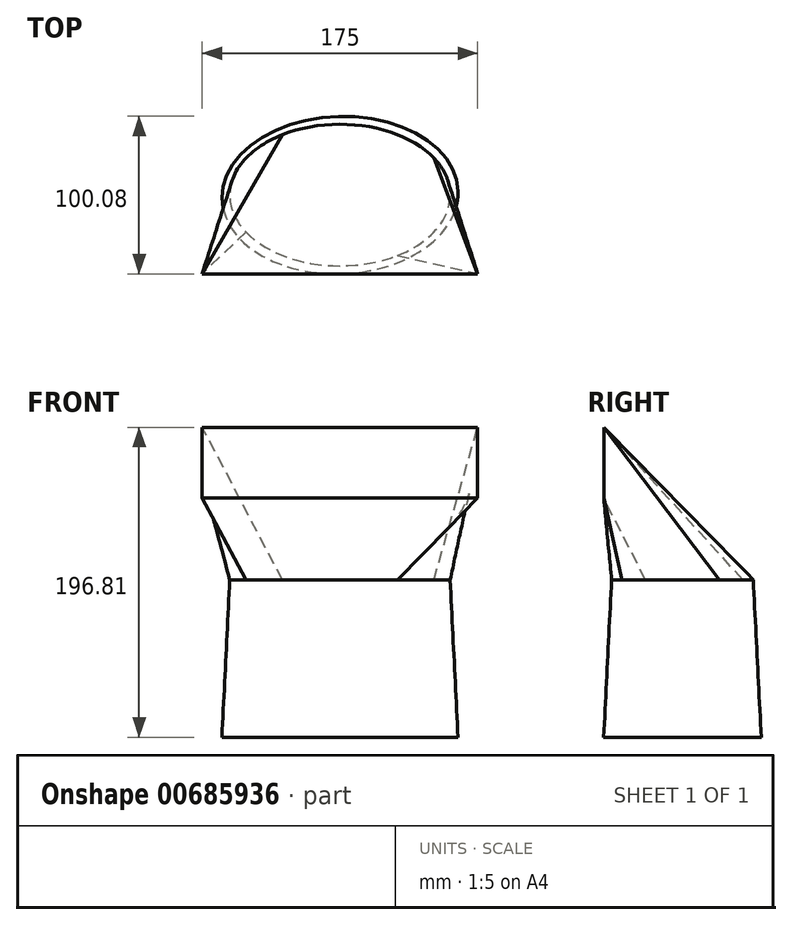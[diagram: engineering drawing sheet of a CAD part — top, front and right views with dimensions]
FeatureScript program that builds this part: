
annotation { "Feature Type Name" : "Feature", "Feature Type Description" : "" }
export const myFeature = defineFeature(function(context is Context, id is Id, definition is map)
    precondition{}
    {
        {
            assignVariable(context, id + "F0", {"name" : "X", "anyValue" : 1});
        }
        {
            var Q0;
            Q0=qCreatedBy(makeId("Top.planeOp"),FACE);
            var sketch = newSketch(context, id + "F1", { "sketchPlane" : qUnion([Q0])});
            skEllipse(sketch, "E0", {"center": v(0, 0) * mm, "majorRadius": 75 * mm, "minorRadius": 50 * mm, "majorAxis": v(1, 0.04)});
            skSolve(sketch);
        }
        {
            var Q0;
            Q0=qCreatedBy(makeId("Top.planeOp"),FACE);
            cPlane(context, id + "F2", {"entities" : qUnion([Q0]), "cplaneType" : CPlaneType.OFFSET, "offset" : (getVariable(context, 'X') * 100) * mm, "width" : 150 * mm, "height" : 150 * mm});
        }
        {
            var Q0;
            Q0=qCreatedBy(id+"F2.planeOp",FACE);
            var sketch = newSketch(context, id + "F3", { "sketchPlane" : qUnion([Q0])});
            skEllipse(sketch, "E1", {"center": v(0, 0) * mm, "majorRadius": 70 * mm, "minorRadius": 45 * mm, "majorAxis": v(-1, 0)});
            skSolve(sketch);
        }
        {
            var Q0;
            Q0=makeQuery(id+"F1.imprint","IMPRINT",FACE,{"disambiguationData":[TD([[makeQuery(id+"F1.imprint","IMPRINT",EDGE,{"derivedFrom":sQuery(id+"F1.wireOp",EDGE,"E0")}),1.0]])]});
            var Q1;
            Q1=makeQuery(id+"F3.imprint","IMPRINT",FACE,{"disambiguationData":[TD([[makeQuery(id+"F3.imprint","IMPRINT",EDGE,{"derivedFrom":sQuery(id+"F3.wireOp",EDGE,"E1")}),1.0]])]});
            loft(context, id + "F4", {"sheetProfilesArray" : [{ "sheetProfileEntities" : qUnion([Q0]) }, { "sheetProfileEntities" : qUnion([Q1]) }]});
        }
        {
            var Q0;
            Q0=qCreatedBy(makeId("Front.planeOp"),FACE);
            var sketch = newSketch(context, id + "F5", { "sketchPlane" : qUnion([Q0])});
            skLineSegment(sketch, "E2.bottom", {"start": v(-87.5, 196.8) * mm, "end": v(87.5, 196.8) * mm});
            skLineSegment(sketch, "E2.top", {"start": v(-87.5, 151.8) * mm, "end": v(87.5, 151.8) * mm});
            skLineSegment(sketch, "E2.left", {"start": v(-87.5, 196.8) * mm, "end": v(-87.5, 151.8) * mm});
            skLineSegment(sketch, "E2.right", {"start": v(87.5, 196.8) * mm, "end": v(87.5, 151.8) * mm});
            skPoint(sketch, "E3", {"position": v(-63.7, 88.78) * mm});
            skLineSegment(sketch, "E4", {"start": v(0, 196.8) * mm, "end": v(0, 151.8) * mm});
            skLineSegment(sketch, "E5", {"start": v(0, 174.3) * mm, "end": v(87.5, 174.3) * mm});
            skLineSegment(sketch, "E6", {"start": v(0, 174.3) * mm, "end": v(-87.5, 174.3) * mm});
            skSolve(sketch);
        }
        {
            var Q0;
            {var subQ5=sQuery(id+"F5.wireOp",EDGE,"E5");Q0=makeQuery(id+"F5.imprint","IMPRINT",FACE,{"disambiguationData":[TD([[makeQuery(id+"F5.imprint","IMPRINT",EDGE,{"derivedFrom":subQ5}),-1.0]])]});}
            cPlane(context, id + "F6", {"entities" : qUnion([Q0]), "cplaneType" : CPlaneType.OFFSET, "offset" : 50 * mm, "width" : 150 * mm, "height" : 150 * mm});
        }
        {
            var Q0;
            Q0=qCreatedBy(id+"F6.planeOp",FACE);
            var sketch = newSketch(context, id + "F7", { "sketchPlane" : qUnion([Q0])});
            skLineSegment(sketch, "E7.bottom", {"start": v(-87.5, 196.8) * mm, "end": v(87.5, 196.8) * mm});
            skLineSegment(sketch, "E7.top", {"start": v(-87.5, 151.8) * mm, "end": v(87.5, 151.8) * mm});
            skLineSegment(sketch, "E7.left", {"start": v(-87.5, 196.8) * mm, "end": v(-87.5, 151.8) * mm});
            skLineSegment(sketch, "E7.right", {"start": v(87.5, 196.8) * mm, "end": v(87.5, 151.8) * mm});
            skSolve(sketch);
        }
        {
            var Q0;
            Q0=makeQuery(id+"F4.opLoft","CAP_FACE",FACE,{"disambiguationData":[OSD([makeQuery(id+"F3.imprint","IMPRINT",FACE,{"disambiguationData":[TD([[makeQuery(id+"F3.imprint","IMPRINT",EDGE,{"derivedFrom":sQuery(id+"F3.wireOp",EDGE,"E1")}),1.0]])]})])],"isStart":true});
            var Q1;
            Q1=makeQuery(id+"F7.imprint","IMPRINT",FACE,{"disambiguationData":[TD([[makeQuery(id+"F7.imprint","IMPRINT",EDGE,{"derivedFrom":sQuery(id+"F7.wireOp",EDGE,"E7.bottom")}),-1.0]])]});
            loft(context, id + "F8", {"operationType" : NewBodyOperationType.ADD, "sheetProfilesArray" : [{ "sheetProfileEntities" : qUnion([Q0]) }, { "sheetProfileEntities" : qUnion([Q1]) }]});
        }
    });
